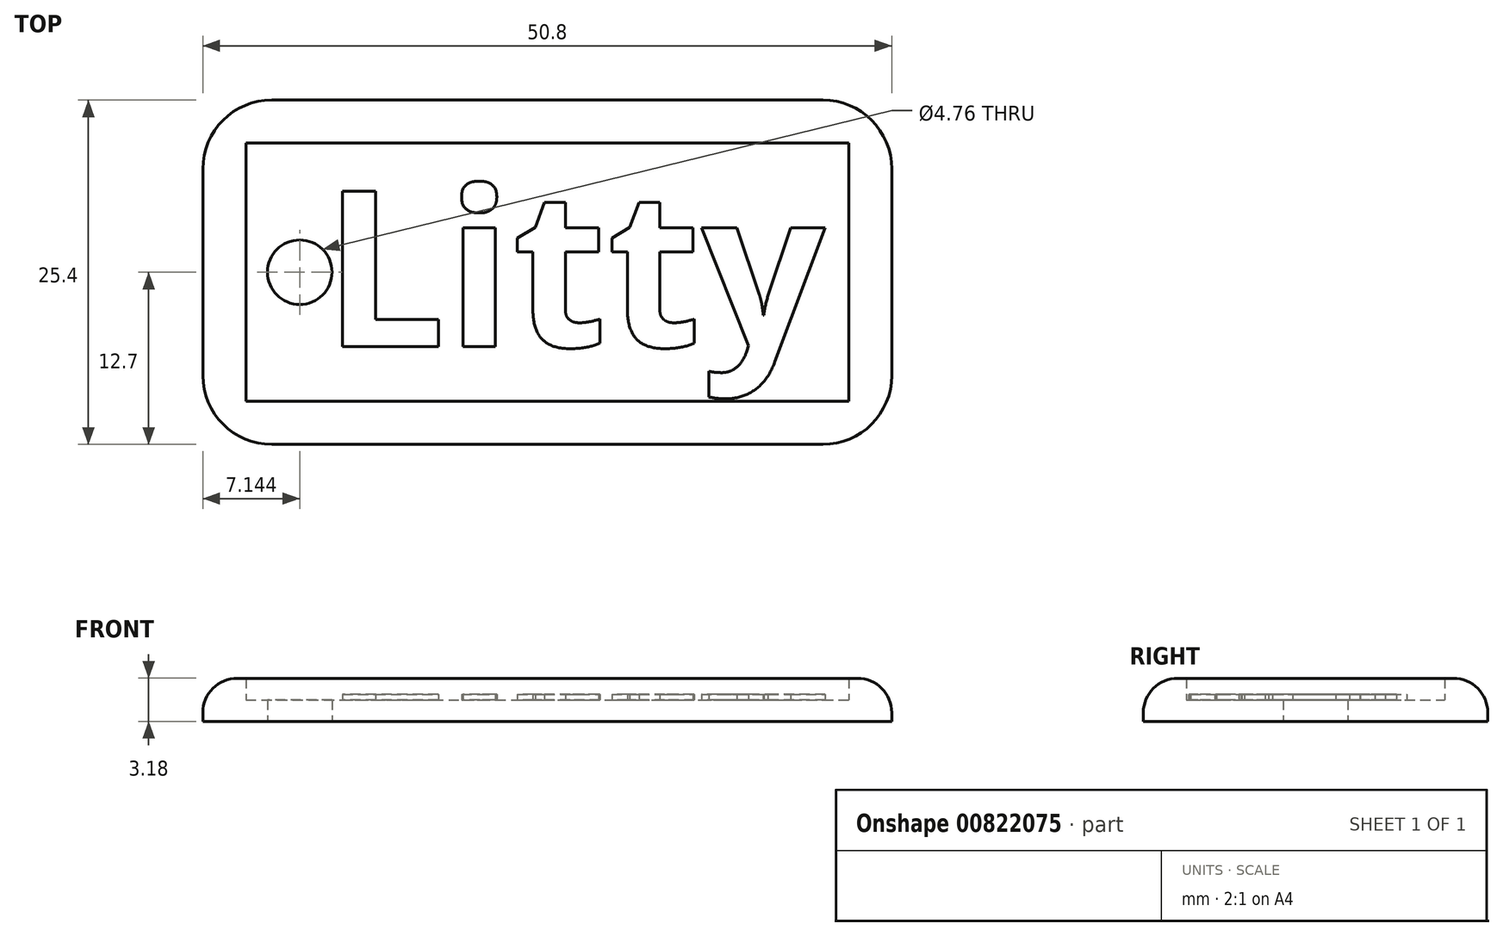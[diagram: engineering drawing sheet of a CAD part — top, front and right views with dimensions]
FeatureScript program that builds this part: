
annotation { "Feature Type Name" : "Feature", "Feature Type Description" : "" }
export const myFeature = defineFeature(function(context is Context, id is Id, definition is map)
    precondition{}
    {
        {
            var Q0;
            Q0=qCreatedBy(makeId("Top.planeOp"),FACE);
            var sketch = newSketch(context, id + "F0", { "sketchPlane" : qUnion([Q0])});
            skLineSegment(sketch, "E0.bottom", {"start": v(0, 0) * mm, "end": v(50.8, 0) * mm});
            skLineSegment(sketch, "E0.top", {"start": v(0, 25.4) * mm, "end": v(50.8, 25.4) * mm});
            skLineSegment(sketch, "E0.left", {"start": v(0, 0) * mm, "end": v(0, 25.4) * mm});
            skLineSegment(sketch, "E0.right", {"start": v(50.8, 0) * mm, "end": v(50.8, 25.4) * mm});
            skCircle(sketch, "E1", {"center": v(7.14, 12.7) * mm, "radius": 2.38 * mm});
            skPoint(sketch, "E1.centerSnap0", {"position": v(0, 12.7) * mm});
            skLineSegment(sketch, "E2.0", {"start": v(3.18, 3.18) * mm, "end": v(47.62, 3.18) * mm});
            skLineSegment(sketch, "E2.1", {"start": v(3.17, 3.18) * mm, "end": v(3.17, 22.22) * mm});
            skLineSegment(sketch, "E2.2", {"start": v(3.17, 22.23) * mm, "end": v(47.62, 22.23) * mm});
            skLineSegment(sketch, "E2.3", {"start": v(47.62, 3.18) * mm, "end": v(47.62, 22.23) * mm});
            skSolve(sketch);
        }
        {
            var Q0;
            Q0=makeQuery(id+"F0.imprint","IMPRINT",FACE,{"disambiguationData":[TD([[makeQuery(id+"F0.imprint","IMPRINT",EDGE,{"derivedFrom":sQuery(id+"F0.wireOp",EDGE,"E1")}),-1.0]])]});
            extrude(context, id + "F1", {"entities" : qUnion([Q0]), "depth" : 1.59 * mm, "offsetDistance" : 25.4 * mm});
        }
        {
            var Q0;
            Q0 = qSketchRegion(id + "F0", true);
            extrude(context, id + "F2", {"entities" : qUnion([Q0]), "operationType" : NewBodyOperationType.ADD, "depth" : 3.17 * mm, "offsetDistance" : 25.4 * mm});
        }
        {
            var Q0;
            Q0=makeQuery(id+"F2.opExtrude","SWEPT_EDGE",EDGE,{"disambiguationData":[OSD([sQuery(id+"F0.wireOp",EDGE,"E0.top"),sQuery(id+"F0.wireOp",EDGE,"E0.right")])]});
            var Q1;
            Q1=makeQuery(id+"F2.opExtrude","SWEPT_EDGE",EDGE,{"disambiguationData":[OSD([sQuery(id+"F0.wireOp",EDGE,"E0.bottom"),sQuery(id+"F0.wireOp",EDGE,"E0.right")])]});
            var Q2;
            Q2=makeQuery(id+"F2.opExtrude","SWEPT_EDGE",EDGE,{"disambiguationData":[OSD([sQuery(id+"F0.wireOp",EDGE,"E0.bottom"),sQuery(id+"F0.wireOp",EDGE,"E0.left")])]});
            var Q3;
            Q3=makeQuery(id+"F2.opExtrude","SWEPT_EDGE",EDGE,{"disambiguationData":[OSD([sQuery(id+"F0.wireOp",EDGE,"E0.top"),sQuery(id+"F0.wireOp",EDGE,"E0.left")])]});
            fillet(context, id + "F3", {"entities" : qUnion([Q0, Q1, Q2, Q3]), "radius" : 5.08 * mm, "tangentPropagation" : true, "allowEdgeOverflow" : false});
        }
        {
            var Q0;
            Q0=makeQuery(id+"F2.opExtrude","CAP_EDGE",EDGE,{"disambiguationData":[OSD([sQuery(id+"F0.wireOp",EDGE,"E0.bottom")])],"isStart":false});
            fillet(context, id + "F4", {"entities" : qUnion([Q0]), "radius" : 2.54 * mm, "tangentPropagation" : true, "allowEdgeOverflow" : false});
        }
        {
            var Q0;
            Q0=makeQuery(id+"F1.opExtrude","CAP_FACE",FACE,{"disambiguationData":[OSD([sQuery(id+"F0.wireOp",EDGE,"E1"),sQuery(id+"F0.wireOp",EDGE,"E2.0"),sQuery(id+"F0.wireOp",EDGE,"E2.1"),sQuery(id+"F0.wireOp",EDGE,"E2.2"),sQuery(id+"F0.wireOp",EDGE,"E2.3")])],"isStart":false});
            var sketch = newSketch(context, id + "F5", { "sketchPlane" : qUnion([Q0])});
            skText(sketch, "E3", { "text": "Litty", "fontName": "OpenSans-Bold.ttf"});
            const initialGuessF5  = {"E3": [0.00885, 0.00722, 1, 0, 0.01156]};
            skSetInitialGuess(sketch, initialGuessF5);
            skSolve(sketch);
        }
        {
            var Q0;
            Q0 = qSketchRegion(id + "F5", true);
            extrude(context, id + "F6", {"entities" : qUnion([Q0]), "operationType" : NewBodyOperationType.ADD, "depth" : 0.4 * mm, "offsetDistance" : 25.4 * mm});
        }
    });
